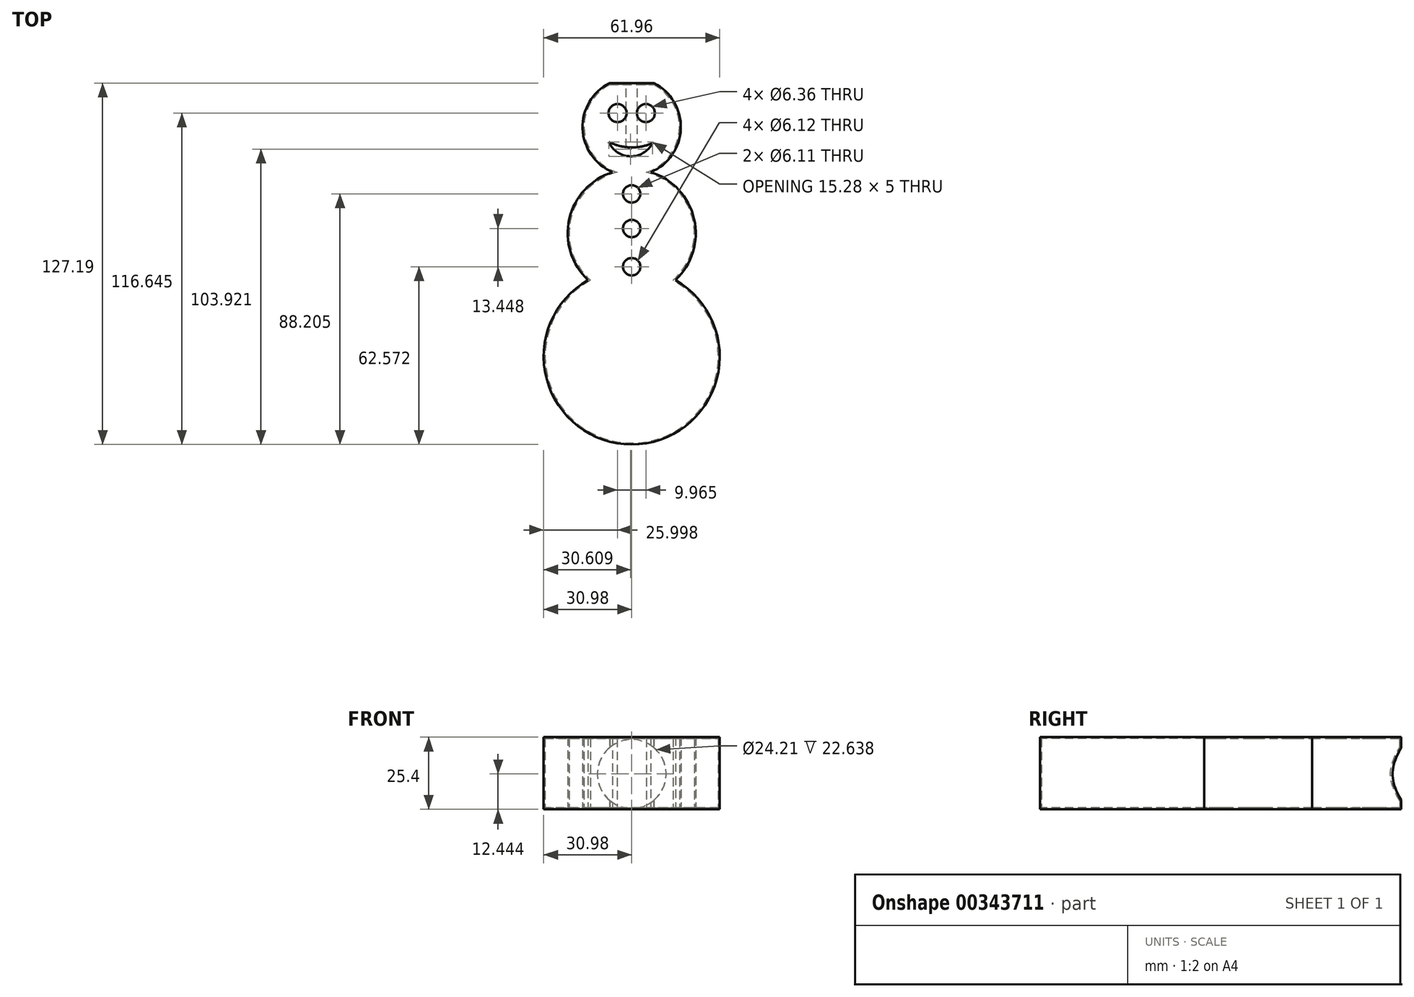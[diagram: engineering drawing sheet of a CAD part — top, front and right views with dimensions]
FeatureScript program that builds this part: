
annotation { "Feature Type Name" : "Feature", "Feature Type Description" : "" }
export const myFeature = defineFeature(function(context is Context, id is Id, definition is map)
    precondition{}
    {
        {
            var Q0;
            Q0=qCreatedBy(makeId("Top.planeOp"),FACE);
            var sketch = newSketch(context, id + "F0", { "sketchPlane" : qUnion([Q0])});
            skCircle(sketch, "E0", {"center": v(0, 37.43) * mm, "radius": 17.3 * mm});
            skCircle(sketch, "E1", {"center": v(0, 0) * mm, "radius": 22.54 * mm});
            skCircle(sketch, "E2", {"center": v(0, -43.36) * mm, "radius": 30.98 * mm});
            skSolve(sketch);
        }
        {
            var Q0;
            {var subQ0=sQuery(id+"F0.wireOp",EDGE,"E1");var subQ1=sQuery(id+"F0.wireOp",EDGE,"E0");var subQ2=makeQuery(id+"F0.imprint","INTERSECT",VERTEX,{"disambiguationData":[OD(0.0)],"derivedFrom":[subQ1,subQ0]});Q0=makeQuery(id+"F0.imprint","IMPRINT",FACE,{"disambiguationData":[TD([[makeQuery(id+"F0.imprint","IMPRINT",EDGE,{"disambiguationData":[TD([[subQ2,1.0]])],"derivedFrom":subQ1}),1.0]])]});}
            var Q1;
            {var subQ0=sQuery(id+"F0.wireOp",EDGE,"E2");var subQ1=sQuery(id+"F0.wireOp",EDGE,"E1");var subQ2=makeQuery(id+"F0.imprint","INTERSECT",VERTEX,{"disambiguationData":[OD(0.0)],"derivedFrom":[subQ1,subQ0]});Q1=makeQuery(id+"F0.imprint","IMPRINT",FACE,{"disambiguationData":[TD([[makeQuery(id+"F0.imprint","IMPRINT",EDGE,{"disambiguationData":[TD([[subQ2,-1.0]])],"derivedFrom":subQ1}),-1.0]])]});}
            var Q2;
            {var subQ0=sQuery(id+"F0.wireOp",EDGE,"E1");var subQ1=sQuery(id+"F0.wireOp",EDGE,"E0");var subQ2=makeQuery(id+"F0.imprint","INTERSECT",VERTEX,{"disambiguationData":[OD(0.0)],"derivedFrom":[subQ1,subQ0]});Q2=makeQuery(id+"F0.imprint","IMPRINT",FACE,{"disambiguationData":[TD([[makeQuery(id+"F0.imprint","IMPRINT",EDGE,{"disambiguationData":[TD([[subQ2,-1.0]])],"derivedFrom":subQ1}),1.0]])]});}
            var Q3;
            {var subQ0=sQuery(id+"F0.wireOp",EDGE,"E1");var subQ1=sQuery(id+"F0.wireOp",EDGE,"E0");var subQ2=makeQuery(id+"F0.imprint","INTERSECT",VERTEX,{"disambiguationData":[OD(0.0)],"derivedFrom":[subQ1,subQ0]});Q3=makeQuery(id+"F0.imprint","IMPRINT",FACE,{"disambiguationData":[TD([[makeQuery(id+"F0.imprint","IMPRINT",EDGE,{"disambiguationData":[TD([[subQ2,-1.0]])],"derivedFrom":subQ1}),-1.0]])]});}
            var Q4;
            {var subQ0=sQuery(id+"F0.wireOp",EDGE,"E2");var subQ1=sQuery(id+"F0.wireOp",EDGE,"E1");var subQ2=makeQuery(id+"F0.imprint","INTERSECT",VERTEX,{"disambiguationData":[OD(0.0)],"derivedFrom":[subQ1,subQ0]});Q4=makeQuery(id+"F0.imprint","IMPRINT",FACE,{"disambiguationData":[TD([[makeQuery(id+"F0.imprint","IMPRINT",EDGE,{"disambiguationData":[TD([[subQ2,-1.0]])],"derivedFrom":subQ1}),1.0]])]});}
            extrude(context, id + "F1", {"entities" : qUnion([Q0, Q1, Q2, Q3, Q4]), "depth" : 25.4 * mm});
        }
        {
            var Q0;
            Q0=qCreatedBy(makeId("Top.planeOp"),FACE);
            var sketch = newSketch(context, id + "F2", { "sketchPlane" : qUnion([Q0])});
            skLineSegment(sketch, "E3.bottom", {"start": v(-12.28, 52.85) * mm, "end": v(12.28, 52.85) * mm});
            skLineSegment(sketch, "E3.top", {"start": v(-12.28, 55.76) * mm, "end": v(12.28, 55.76) * mm});
            skLineSegment(sketch, "E3.left", {"start": v(-12.28, 52.85) * mm, "end": v(-12.28, 55.76) * mm});
            skLineSegment(sketch, "E3.right", {"start": v(12.28, 52.85) * mm, "end": v(12.28, 55.76) * mm});
            skSolve(sketch);
        }
        {
            var Q0;
            Q0=makeQuery(id+"F2.imprint","IMPRINT",FACE,{"disambiguationData":[TD([[makeQuery(id+"F2.imprint","IMPRINT",EDGE,{"derivedFrom":sQuery(id+"F2.wireOp",EDGE,"E3.bottom")}),1.0]])]});
            extrude(context, id + "F3", {"entities" : qUnion([Q0]), "operationType" : NewBodyOperationType.REMOVE, "depth" : 25.4 * mm});
        }
        {
            var Q0;
            Q0=makeQuery(id+"F3.boolean.opBoolean","COPY",FACE,{"derivedFrom":makeQuery(id+"F3.opExtrude","SWEPT_FACE",FACE,{"disambiguationData":[OSD([sQuery(id+"F2.wireOp",EDGE,"E3.bottom")])]})});
            var Q1;
            Q1=makeQuery(id+"F1.opExtrude","SWEPT_BODY",BODY,{"disambiguationData":[OSD([sQuery(id+"F0.wireOp",EDGE,"E0"),sQuery(id+"F0.wireOp",EDGE,"E1"),sQuery(id+"F0.wireOp",EDGE,"E2")])]});
            shell(context, id + "F4", {"isHollow" : true, "entities" : qUnion([Q0]), "parts" : qUnion([Q1]), "thickness" : .5 * mm});
        }
        {
            var Q0;
            Q0=makeQuery(id+"F1.opExtrude","CAP_FACE",FACE,{"disambiguationData":[OSD([sQuery(id+"F0.wireOp",EDGE,"E0"),sQuery(id+"F0.wireOp",EDGE,"E1"),sQuery(id+"F0.wireOp",EDGE,"E2")])],"isStart":false});
            var sketch = newSketch(context, id + "F5", { "sketchPlane" : qUnion([Q0])});
            skCircle(sketch, "E4", {"center": v(0, 13.86) * mm, "radius": 3.06 * mm});
            skCircle(sketch, "E5", {"center": v(0, 1.68) * mm, "radius": 3.06 * mm});
            skCircle(sketch, "E6", {"center": v(0, -11.77) * mm, "radius": 3.06 * mm});
            skSolve(sketch);
        }
        {
            var Q0;
            Q0=makeQuery(id+"F5.imprint","IMPRINT",FACE,{"disambiguationData":[TD([[makeQuery(id+"F5.imprint","IMPRINT",EDGE,{"derivedFrom":sQuery(id+"F5.wireOp",EDGE,"E4")}),-1.0]])]});
            var sketch = newSketch(context, id + "F6", { "sketchPlane" : qUnion([Q0])});
            skCircle(sketch, "E7", {"center": v(-4.98, 42.3) * mm, "radius": 3.18 * mm});
            skCircle(sketch, "E8.MirrorC", {"center": v(4.98, 42.3) * mm, "radius": 3.18 * mm});
            skSolve(sketch);
        }
        {
            var Q0;
            Q0=makeQuery(id+"F6.imprint","IMPRINT",FACE,{"disambiguationData":[TD([[makeQuery(id+"F6.imprint","IMPRINT",EDGE,{"derivedFrom":sQuery(id+"F6.wireOp",EDGE,"E7")}),-1.0]])]});
            var sketch = newSketch(context, id + "F7", { "sketchPlane" : qUnion([Q0])});
            skArc(sketch, "E9", {"start": v(-8.01, 32.08) * mm, "mid": v(-0.5, 27.08) * mm, "end": v(7.27, 31.7) * mm});
            skArc(sketch, "E10", {"start": v(-8.01, 32.08) * mm, "mid": v(-0.41, 30.22) * mm, "end": v(7.27, 31.7) * mm});
            skSolve(sketch);
        }
        {
            var Q0;
            Q0 = qSketchRegion(id + "F5", true);
            var Q1;
            Q1 = qSketchRegion(id + "F6", true);
            var Q2;
            Q2 = qSketchRegion(id + "F7", true);
            extrude(context, id + "F8", {"entities" : qUnion([Q0, Q1, Q2]), "operationType" : NewBodyOperationType.REMOVE, "oppositeDirection" : true, "depth" : 25.4 * mm});
        }
        {
            var Q0;
            Q0=makeQuery(id+"F3.boolean.opBoolean","COPY",FACE,{"derivedFrom":makeQuery(id+"F3.opExtrude","SWEPT_FACE",FACE,{"disambiguationData":[OSD([sQuery(id+"F2.wireOp",EDGE,"E3.bottom")])]})});
            var sketch = newSketch(context, id + "F9", { "sketchPlane" : qUnion([Q0])});
            skCircle(sketch, "E11", {"center": v(0, 12.44) * mm, "radius": 12.1 * mm});
            skSolve(sketch);
        }
        {
            var Q0;
            Q0 = qSketchRegion(id + "F9", true);
            extrude(context, id + "F10", {"entities" : qUnion([Q0]), "operationType" : NewBodyOperationType.REMOVE, "oppositeDirection" : true, "depth" : 25.4 * mm});
        }
    });
